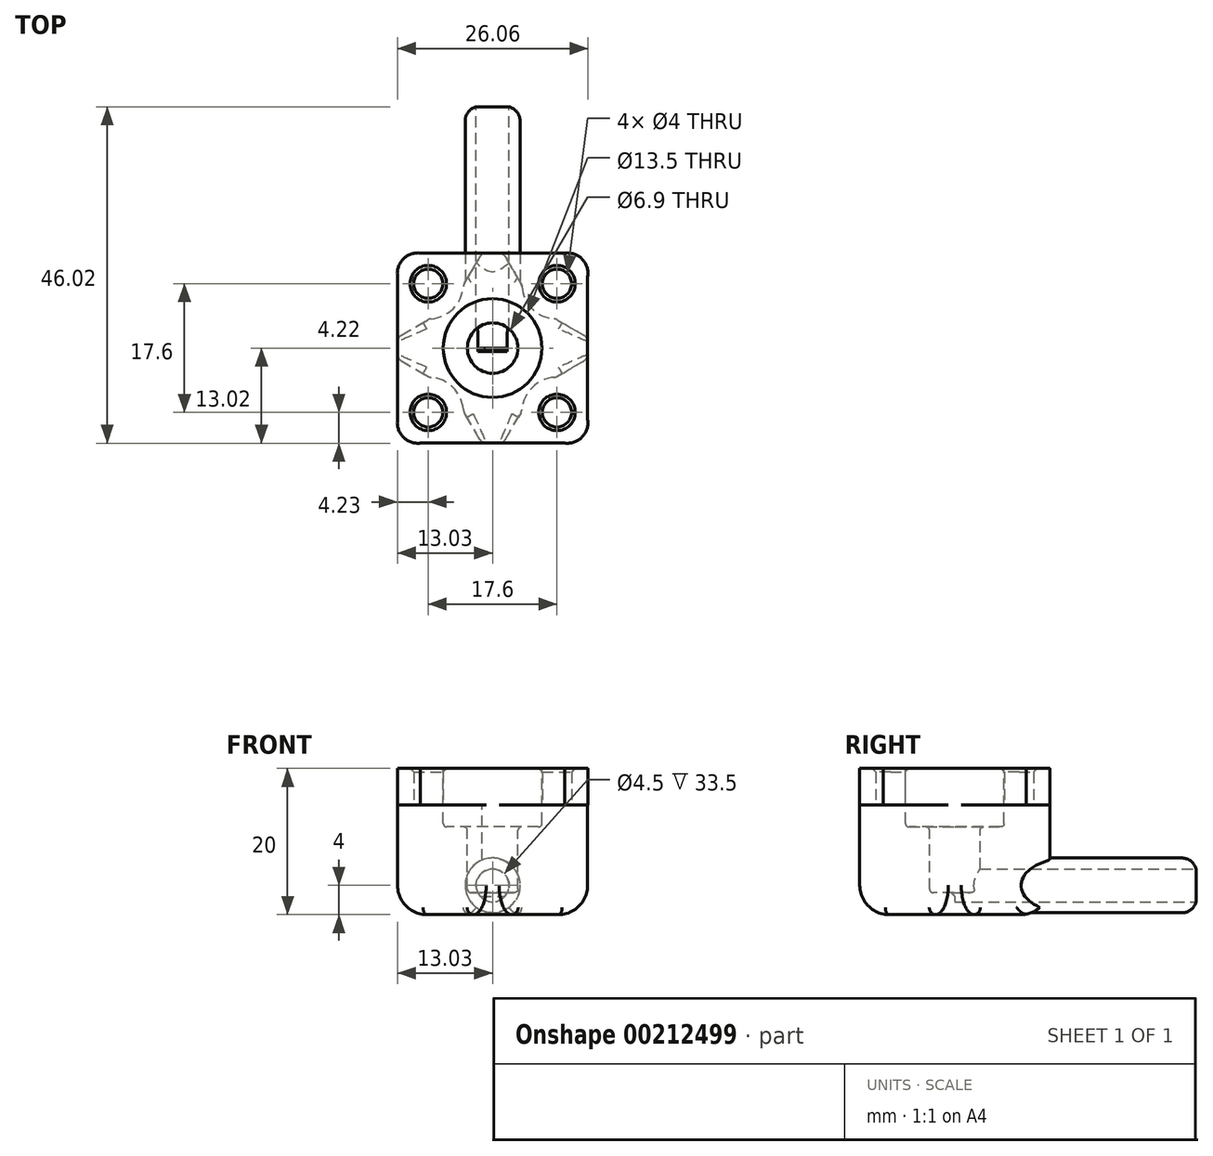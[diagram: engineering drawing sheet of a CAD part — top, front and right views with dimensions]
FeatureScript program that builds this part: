
annotation { "Feature Type Name" : "Feature", "Feature Type Description" : "" }
export const myFeature = defineFeature(function(context is Context, id is Id, definition is map)
    precondition{}
    {
        {
            var Q0;
            Q0=qCreatedBy(makeId("Top.planeOp"),FACE);
            var sketch = newSketch(context, id + "F0", { "sketchPlane" : qUnion([Q0])});
            skLineSegment(sketch, "E0.bottom", {"start": v(-9.87, 13) * mm, "end": v(9.87, 13) * mm});
            skLineSegment(sketch, "E0.top", {"start": v(-9.87, -13) * mm, "end": v(9.87, -13) * mm});
            skLineSegment(sketch, "E0.left", {"start": v(-13, 9.78) * mm, "end": v(-13, -9.78) * mm});
            skLineSegment(sketch, "E0.right", {"start": v(13, 9.78) * mm, "end": v(13, -9.78) * mm});
            skLineSegment(sketch, "E1.bottom", {"start": v(-8.8, 8.8) * mm, "end": v(8.8, 8.8) * mm, "construction": true});
            skLineSegment(sketch, "E1.top", {"start": v(-8.8, -8.8) * mm, "end": v(8.8, -8.8) * mm, "construction": true});
            skLineSegment(sketch, "E1.left", {"start": v(-8.8, 8.8) * mm, "end": v(-8.8, -8.8) * mm, "construction": true});
            skLineSegment(sketch, "E1.right", {"start": v(8.8, 8.8) * mm, "end": v(8.8, -8.8) * mm, "construction": true});
            skCircle(sketch, "E2", {"center": v(-8.8, 8.8) * mm, "radius": 2 * mm});
            skCircle(sketch, "E3", {"center": v(8.8, 8.8) * mm, "radius": 2 * mm});
            skCircle(sketch, "E4", {"center": v(8.8, -8.8) * mm, "radius": 2 * mm});
            skCircle(sketch, "E5", {"center": v(-8.8, -8.8) * mm, "radius": 2 * mm});
            skArc(sketch, "E6", {"start": v(-9.87, 13) * mm, "mid": v(-12.24, 12.17) * mm, "end": v(-13, 9.78) * mm});
            skArc(sketch, "E7.MirrorCS", {"start": v(9.87, 13) * mm, "mid": v(12.24, 12.17) * mm, "end": v(13, 9.78) * mm});
            skArc(sketch, "E8.MirrorCS", {"start": v(-9.87, -13) * mm, "mid": v(-12.24, -12.17) * mm, "end": v(-13, -9.78) * mm});
            skArc(sketch, "E9.MirrorCS", {"start": v(9.87, -13) * mm, "mid": v(12.24, -12.17) * mm, "end": v(13, -9.78) * mm});
            skPoint(sketch, "E10.orphan", {"position": v(13, 13) * mm});
            skPoint(sketch, "E11.orphan", {"position": v(13, -13) * mm});
            skPoint(sketch, "E12.orphan", {"position": v(-13, 13) * mm});
            skPoint(sketch, "E13.orphan", {"position": v(-9.87, 13) * mm});
            skSolve(sketch);
        }
        {
            var Q0;
            Q0 = qSketchRegion(id + "F0", true);
            extrude(context, id + "F1", {"entities" : qUnion([Q0]), "depth" : 20 * mm});
        }
        {
            var Q0;
            Q0=makeQuery(id+"F1.opExtrude","CAP_FACE",FACE,{"disambiguationData":[OSD([sQuery(id+"F0.wireOp",EDGE,"E0.bottom"),sQuery(id+"F0.wireOp",EDGE,"E0.top"),sQuery(id+"F0.wireOp",EDGE,"E0.left"),sQuery(id+"F0.wireOp",EDGE,"E0.right"),sQuery(id+"F0.wireOp",EDGE,"E2"),sQuery(id+"F0.wireOp",EDGE,"E3"),sQuery(id+"F0.wireOp",EDGE,"E4"),sQuery(id+"F0.wireOp",EDGE,"E5"),sQuery(id+"F0.wireOp",EDGE,"E6"),sQuery(id+"F0.wireOp",EDGE,"E7.MirrorCS"),sQuery(id+"F0.wireOp",EDGE,"E8.MirrorCS"),sQuery(id+"F0.wireOp",EDGE,"E9.MirrorCS")])],"isStart":false});
            var sketch = newSketch(context, id + "F2", { "sketchPlane" : qUnion([Q0])});
            skCircle(sketch, "E14", {"center": v(0, 0) * mm, "radius": 3.45 * mm});
            skSolve(sketch);
        }
        {
            var Q0;
            Q0 = qSketchRegion(id + "F2", true);
            extrude(context, id + "F3", {"entities" : qUnion([Q0]), "operationType" : NewBodyOperationType.REMOVE, "oppositeDirection" : true, "depth" : 17 * mm});
        }
        {
            var Q0;
            Q0=makeQuery(id+"F1.opExtrude","CAP_FACE",FACE,{"disambiguationData":[OSD([sQuery(id+"F0.wireOp",EDGE,"E0.bottom"),sQuery(id+"F0.wireOp",EDGE,"E0.top"),sQuery(id+"F0.wireOp",EDGE,"E0.left"),sQuery(id+"F0.wireOp",EDGE,"E0.right"),sQuery(id+"F0.wireOp",EDGE,"E2"),sQuery(id+"F0.wireOp",EDGE,"E3"),sQuery(id+"F0.wireOp",EDGE,"E4"),sQuery(id+"F0.wireOp",EDGE,"E5"),sQuery(id+"F0.wireOp",EDGE,"E6"),sQuery(id+"F0.wireOp",EDGE,"E7.MirrorCS"),sQuery(id+"F0.wireOp",EDGE,"E8.MirrorCS"),sQuery(id+"F0.wireOp",EDGE,"E9.MirrorCS")])],"isStart":false});
            var sketch = newSketch(context, id + "F4", { "sketchPlane" : qUnion([Q0])});
            skCircle(sketch, "E15", {"center": v(0, 0) * mm, "radius": 6.75 * mm});
            skSolve(sketch);
        }
        {
            var Q0;
            Q0 = qSketchRegion(id + "F4", true);
            extrude(context, id + "F5", {"entities" : qUnion([Q0]), "operationType" : NewBodyOperationType.REMOVE, "oppositeDirection" : true, "depth" : 8 * mm});
        }
        {
            var Q0;
            Q0=makeQuery(id+"F1.opExtrude","CAP_FACE",FACE,{"disambiguationData":[OSD([sQuery(id+"F0.wireOp",EDGE,"E0.bottom"),sQuery(id+"F0.wireOp",EDGE,"E0.top"),sQuery(id+"F0.wireOp",EDGE,"E0.left"),sQuery(id+"F0.wireOp",EDGE,"E0.right"),sQuery(id+"F0.wireOp",EDGE,"E2"),sQuery(id+"F0.wireOp",EDGE,"E3"),sQuery(id+"F0.wireOp",EDGE,"E4"),sQuery(id+"F0.wireOp",EDGE,"E5"),sQuery(id+"F0.wireOp",EDGE,"E6"),sQuery(id+"F0.wireOp",EDGE,"E7.MirrorCS"),sQuery(id+"F0.wireOp",EDGE,"E8.MirrorCS"),sQuery(id+"F0.wireOp",EDGE,"E9.MirrorCS")])],"isStart":true});
            var sketch = newSketch(context, id + "F6", { "sketchPlane" : qUnion([Q0])});
            skCircle(sketch, "E16", {"center": v(-8.8, 8.8) * mm, "radius": 4.81 * mm});
            skCircle(sketch, "E17.MirrorC", {"center": v(8.8, 8.8) * mm, "radius": 4.81 * mm});
            skCircle(sketch, "E18.MirrorC", {"center": v(-8.8, -8.8) * mm, "radius": 4.81 * mm});
            skCircle(sketch, "E19.MirrorC", {"center": v(8.8, -8.8) * mm, "radius": 4.81 * mm});
            skSolve(sketch);
        }
        {
            var Q0;
            Q0 = qSketchRegion(id + "F6", true);
            extrude(context, id + "F7", {"entities" : qUnion([Q0]), "operationType" : NewBodyOperationType.REMOVE, "oppositeDirection" : true, "depth" : 30 * mm, "symmetric" : true});
        }
        {
            var Q0;
            Q0=makeQuery(id+"F1.opExtrude","SWEPT_FACE",FACE,{"disambiguationData":[OSD([sQuery(id+"F0.wireOp",EDGE,"E0.bottom")])]});
            var sketch = newSketch(context, id + "F8", { "sketchPlane" : qUnion([Q0])});
            skCircle(sketch, "E20", {"center": v(0, 4) * mm, "radius": 3.75 * mm});
            skSolve(sketch);
        }
        {
            var Q0;
            Q0 = qSketchRegion(id + "F8", true);
            extrude(context, id + "F9", {"entities" : qUnion([Q0]), "operationType" : NewBodyOperationType.ADD, "depth" : 20 * mm});
        }
        {
            var Q0;
            Q0=makeQuery(id+"F9.opExtrude","CAP_FACE",FACE,{"disambiguationData":[OSD([sQuery(id+"F8.wireOp",EDGE,"E20")])],"isStart":false});
            var sketch = newSketch(context, id + "F10", { "sketchPlane" : qUnion([Q0])});
            skCircle(sketch, "E21", {"center": v(0, 4) * mm, "radius": 2.25 * mm});
            skSolve(sketch);
        }
        {
            var Q0;
            Q0 = qSketchRegion(id + "F10", true);
            extrude(context, id + "F11", {"entities" : qUnion([Q0]), "operationType" : NewBodyOperationType.REMOVE, "oppositeDirection" : true, "depth" : 33 * mm});
        }
        {
            var Q0;
            Q0=makeQuery(id+"F7.boolean.opBoolean","INTERSECT",EDGE,{"derivedFrom":[makeQuery(id+"F1.opExtrude","SWEPT_FACE",FACE,{"disambiguationData":[OSD([sQuery(id+"F0.wireOp",EDGE,"E0.left")])]}),makeQuery(id+"F7.opExtrude","SWEPT_FACE",FACE,{"disambiguationData":[OSD([sQuery(id+"F6.wireOp",EDGE,"E16")])]})]});
            var Q1;
            Q1=makeQuery(id+"F7.boolean.opBoolean","INTERSECT",EDGE,{"derivedFrom":[makeQuery(id+"F1.opExtrude","SWEPT_FACE",FACE,{"disambiguationData":[OSD([sQuery(id+"F0.wireOp",EDGE,"E0.left")])]}),makeQuery(id+"F7.opExtrude","SWEPT_FACE",FACE,{"disambiguationData":[OSD([sQuery(id+"F6.wireOp",EDGE,"E18.MirrorC")])]})]});
            var Q2;
            Q2=makeQuery(id+"F7.boolean.opBoolean","INTERSECT",EDGE,{"derivedFrom":[makeQuery(id+"F1.opExtrude","SWEPT_FACE",FACE,{"disambiguationData":[OSD([sQuery(id+"F0.wireOp",EDGE,"E0.right")])]}),makeQuery(id+"F7.opExtrude","SWEPT_FACE",FACE,{"disambiguationData":[OSD([sQuery(id+"F6.wireOp",EDGE,"E17.MirrorC")])]})]});
            var Q3;
            Q3=makeQuery(id+"F7.boolean.opBoolean","INTERSECT",EDGE,{"derivedFrom":[makeQuery(id+"F1.opExtrude","SWEPT_FACE",FACE,{"disambiguationData":[OSD([sQuery(id+"F0.wireOp",EDGE,"E0.bottom")])]}),makeQuery(id+"F7.opExtrude","SWEPT_FACE",FACE,{"disambiguationData":[OSD([sQuery(id+"F6.wireOp",EDGE,"E18.MirrorC")])]})]});
            var Q4;
            Q4=makeQuery(id+"F7.boolean.opBoolean","INTERSECT",EDGE,{"derivedFrom":[makeQuery(id+"F1.opExtrude","SWEPT_FACE",FACE,{"disambiguationData":[OSD([sQuery(id+"F0.wireOp",EDGE,"E0.bottom")])]}),makeQuery(id+"F7.opExtrude","SWEPT_FACE",FACE,{"disambiguationData":[OSD([sQuery(id+"F6.wireOp",EDGE,"E19.MirrorC")])]})]});
            var Q5;
            Q5=makeQuery(id+"F7.boolean.opBoolean","INTERSECT",EDGE,{"derivedFrom":[makeQuery(id+"F1.opExtrude","SWEPT_FACE",FACE,{"disambiguationData":[OSD([sQuery(id+"F0.wireOp",EDGE,"E0.right")])]}),makeQuery(id+"F7.opExtrude","SWEPT_FACE",FACE,{"disambiguationData":[OSD([sQuery(id+"F6.wireOp",EDGE,"E19.MirrorC")])]})]});
            var Q6;
            Q6=makeQuery(id+"F7.boolean.opBoolean","INTERSECT",EDGE,{"derivedFrom":[makeQuery(id+"F1.opExtrude","SWEPT_FACE",FACE,{"disambiguationData":[OSD([sQuery(id+"F0.wireOp",EDGE,"E0.top")])]}),makeQuery(id+"F7.opExtrude","SWEPT_FACE",FACE,{"disambiguationData":[OSD([sQuery(id+"F6.wireOp",EDGE,"E16")])]})]});
            var Q7;
            Q7=makeQuery(id+"F7.boolean.opBoolean","INTERSECT",EDGE,{"derivedFrom":[makeQuery(id+"F1.opExtrude","SWEPT_FACE",FACE,{"disambiguationData":[OSD([sQuery(id+"F0.wireOp",EDGE,"E0.top")])]}),makeQuery(id+"F7.opExtrude","SWEPT_FACE",FACE,{"disambiguationData":[OSD([sQuery(id+"F6.wireOp",EDGE,"E17.MirrorC")])]})]});
            chamfer(context, id + "F12", {"entities" : qUnion([Q0, Q1, Q2, Q3, Q4, Q5, Q6, Q7]), "width" : 5 * mm, "tangentPropagation" : true});
        }
        {
            var Q0;
            Q0=makeQuery(id+"F1.opExtrude","CAP_EDGE",EDGE,{"disambiguationData":[OSD([sQuery(id+"F0.wireOp",EDGE,"E0.right")])],"isStart":true});
            var Q1;
            Q1=makeQuery(id+"F1.opExtrude","CAP_EDGE",EDGE,{"disambiguationData":[OSD([sQuery(id+"F0.wireOp",EDGE,"E0.top")])],"isStart":true});
            var Q2;
            Q2=makeQuery(id+"F1.opExtrude","CAP_EDGE",EDGE,{"disambiguationData":[OSD([sQuery(id+"F0.wireOp",EDGE,"E0.left")])],"isStart":true});
            var Q3;
            Q3=makeQuery(id+"F1.opExtrude","CAP_EDGE",EDGE,{"disambiguationData":[OSD([sQuery(id+"F0.wireOp",EDGE,"E0.bottom")])],"isStart":true});
            fillet(context, id + "F13", {"entities" : qUnion([Q0, Q1, Q2, Q3]), "radius" : 4 * mm, "tangentPropagation" : true, "allowEdgeOverflow" : false});
        }
        {
            var Q0;
            Q0=makeQuery(id+"F9.opExtrude","CAP_EDGE",EDGE,{"disambiguationData":[OSD([sQuery(id+"F8.wireOp",EDGE,"E20")])],"isStart":false});
            fillet(context, id + "F14", {"entities" : qUnion([Q0]), "radius" : 2 * mm, "tangentPropagation" : true, "allowEdgeOverflow" : false});
        }
        {
            var Q0;
            {var subQ0=makeQuery(id+"F1.opExtrude","SWEPT_FACE",FACE,{"disambiguationData":[OSD([sQuery(id+"F0.wireOp",EDGE,"E0.left")])]});Q0=makeQuery(id+"F12.opChamfer","BLEND_EDGE",EDGE,{"blendedFrom":[makeQuery(id+"F7.boolean.opBoolean","INTERSECT",EDGE,{"derivedFrom":[subQ0,makeQuery(id+"F7.opExtrude","SWEPT_FACE",FACE,{"disambiguationData":[OSD([sQuery(id+"F6.wireOp",EDGE,"E18.MirrorC")])]})]}),subQ0],"blendedInto":[subQ0]});}
            var Q1;
            {var subQ0=makeQuery(id+"F1.opExtrude","SWEPT_FACE",FACE,{"disambiguationData":[OSD([sQuery(id+"F0.wireOp",EDGE,"E0.left")])]});Q1=makeQuery(id+"F12.opChamfer","BLEND_EDGE",EDGE,{"blendedFrom":[makeQuery(id+"F7.boolean.opBoolean","INTERSECT",EDGE,{"derivedFrom":[subQ0,makeQuery(id+"F7.opExtrude","SWEPT_FACE",FACE,{"disambiguationData":[OSD([sQuery(id+"F6.wireOp",EDGE,"E16")])]})]}),subQ0],"blendedInto":[subQ0]});}
            var Q2;
            {var subQ0=makeQuery(id+"F7.opExtrude","SWEPT_FACE",FACE,{"disambiguationData":[OSD([sQuery(id+"F6.wireOp",EDGE,"E18.MirrorC")])]});Q2=makeQuery(id+"F12.opChamfer","BLEND_EDGE",EDGE,{"blendedFrom":[makeQuery(id+"F7.boolean.opBoolean","INTERSECT",EDGE,{"derivedFrom":[makeQuery(id+"F1.opExtrude","SWEPT_FACE",FACE,{"disambiguationData":[OSD([sQuery(id+"F0.wireOp",EDGE,"E0.bottom")])]}),subQ0]}),makeQuery(id+"F7.boolean.opBoolean","COPY",FACE,{"derivedFrom":subQ0})],"blendedInto":[makeQuery(id+"F7.boolean.opBoolean","COPY",FACE,{"derivedFrom":subQ0})]});}
            var Q3;
            {var subQ0=makeQuery(id+"F1.opExtrude","SWEPT_FACE",FACE,{"disambiguationData":[OSD([sQuery(id+"F0.wireOp",EDGE,"E0.top")])]});Q3=makeQuery(id+"F12.opChamfer","BLEND_EDGE",EDGE,{"blendedFrom":[makeQuery(id+"F7.boolean.opBoolean","INTERSECT",EDGE,{"derivedFrom":[subQ0,makeQuery(id+"F7.opExtrude","SWEPT_FACE",FACE,{"disambiguationData":[OSD([sQuery(id+"F6.wireOp",EDGE,"E16")])]})]}),subQ0],"blendedInto":[subQ0]});}
            var Q4;
            {var subQ0=makeQuery(id+"F1.opExtrude","SWEPT_FACE",FACE,{"disambiguationData":[OSD([sQuery(id+"F0.wireOp",EDGE,"E0.top")])]});Q4=makeQuery(id+"F12.opChamfer","BLEND_EDGE",EDGE,{"blendedFrom":[makeQuery(id+"F7.boolean.opBoolean","INTERSECT",EDGE,{"derivedFrom":[subQ0,makeQuery(id+"F7.opExtrude","SWEPT_FACE",FACE,{"disambiguationData":[OSD([sQuery(id+"F6.wireOp",EDGE,"E17.MirrorC")])]})]}),subQ0],"blendedInto":[subQ0]});}
            var Q5;
            {var subQ0=makeQuery(id+"F1.opExtrude","SWEPT_FACE",FACE,{"disambiguationData":[OSD([sQuery(id+"F0.wireOp",EDGE,"E0.right")])]});Q5=makeQuery(id+"F12.opChamfer","BLEND_EDGE",EDGE,{"blendedFrom":[makeQuery(id+"F7.boolean.opBoolean","INTERSECT",EDGE,{"derivedFrom":[subQ0,makeQuery(id+"F7.opExtrude","SWEPT_FACE",FACE,{"disambiguationData":[OSD([sQuery(id+"F6.wireOp",EDGE,"E17.MirrorC")])]})]}),subQ0],"blendedInto":[subQ0]});}
            var Q6;
            {var subQ0=makeQuery(id+"F1.opExtrude","SWEPT_FACE",FACE,{"disambiguationData":[OSD([sQuery(id+"F0.wireOp",EDGE,"E0.right")])]});Q6=makeQuery(id+"F12.opChamfer","BLEND_EDGE",EDGE,{"blendedFrom":[makeQuery(id+"F7.boolean.opBoolean","INTERSECT",EDGE,{"derivedFrom":[subQ0,makeQuery(id+"F7.opExtrude","SWEPT_FACE",FACE,{"disambiguationData":[OSD([sQuery(id+"F6.wireOp",EDGE,"E19.MirrorC")])]})]}),subQ0],"blendedInto":[subQ0]});}
            var Q7;
            {var subQ0=makeQuery(id+"F1.opExtrude","SWEPT_FACE",FACE,{"disambiguationData":[OSD([sQuery(id+"F0.wireOp",EDGE,"E0.bottom")])]});Q7=makeQuery(id+"F12.opChamfer","BLEND_EDGE",EDGE,{"disambiguationData":[OD(0.0)],"blendedFrom":[makeQuery(id+"F7.boolean.opBoolean","INTERSECT",EDGE,{"derivedFrom":[subQ0,makeQuery(id+"F7.opExtrude","SWEPT_FACE",FACE,{"disambiguationData":[OSD([sQuery(id+"F6.wireOp",EDGE,"E19.MirrorC")])]})]}),subQ0],"blendedInto":[subQ0]});}
            var Q8;
            {var subQ0=makeQuery(id+"F7.opExtrude","SWEPT_FACE",FACE,{"disambiguationData":[OSD([sQuery(id+"F6.wireOp",EDGE,"E16")])]});Q8=makeQuery(id+"F12.opChamfer","BLEND_EDGE",EDGE,{"blendedFrom":[makeQuery(id+"F7.boolean.opBoolean","INTERSECT",EDGE,{"derivedFrom":[makeQuery(id+"F1.opExtrude","SWEPT_FACE",FACE,{"disambiguationData":[OSD([sQuery(id+"F0.wireOp",EDGE,"E0.left")])]}),subQ0]}),makeQuery(id+"F7.boolean.opBoolean","COPY",FACE,{"derivedFrom":subQ0})],"blendedInto":[makeQuery(id+"F7.boolean.opBoolean","COPY",FACE,{"derivedFrom":subQ0})]});}
            var Q9;
            {var subQ0=makeQuery(id+"F7.opExtrude","SWEPT_FACE",FACE,{"disambiguationData":[OSD([sQuery(id+"F6.wireOp",EDGE,"E16")])]});Q9=makeQuery(id+"F12.opChamfer","BLEND_EDGE",EDGE,{"blendedFrom":[makeQuery(id+"F7.boolean.opBoolean","INTERSECT",EDGE,{"derivedFrom":[makeQuery(id+"F1.opExtrude","SWEPT_FACE",FACE,{"disambiguationData":[OSD([sQuery(id+"F0.wireOp",EDGE,"E0.top")])]}),subQ0]}),makeQuery(id+"F7.boolean.opBoolean","COPY",FACE,{"derivedFrom":subQ0})],"blendedInto":[makeQuery(id+"F7.boolean.opBoolean","COPY",FACE,{"derivedFrom":subQ0})]});}
            var Q10;
            {var subQ0=makeQuery(id+"F7.opExtrude","SWEPT_FACE",FACE,{"disambiguationData":[OSD([sQuery(id+"F6.wireOp",EDGE,"E17.MirrorC")])]});Q10=makeQuery(id+"F12.opChamfer","BLEND_EDGE",EDGE,{"blendedFrom":[makeQuery(id+"F7.boolean.opBoolean","INTERSECT",EDGE,{"derivedFrom":[makeQuery(id+"F1.opExtrude","SWEPT_FACE",FACE,{"disambiguationData":[OSD([sQuery(id+"F0.wireOp",EDGE,"E0.right")])]}),subQ0]}),makeQuery(id+"F7.boolean.opBoolean","COPY",FACE,{"derivedFrom":subQ0})],"blendedInto":[makeQuery(id+"F7.boolean.opBoolean","COPY",FACE,{"derivedFrom":subQ0})]});}
            var Q11;
            {var subQ0=makeQuery(id+"F7.opExtrude","SWEPT_FACE",FACE,{"disambiguationData":[OSD([sQuery(id+"F6.wireOp",EDGE,"E17.MirrorC")])]});Q11=makeQuery(id+"F12.opChamfer","BLEND_EDGE",EDGE,{"blendedFrom":[makeQuery(id+"F7.boolean.opBoolean","INTERSECT",EDGE,{"derivedFrom":[makeQuery(id+"F1.opExtrude","SWEPT_FACE",FACE,{"disambiguationData":[OSD([sQuery(id+"F0.wireOp",EDGE,"E0.top")])]}),subQ0]}),makeQuery(id+"F7.boolean.opBoolean","COPY",FACE,{"derivedFrom":subQ0})],"blendedInto":[makeQuery(id+"F7.boolean.opBoolean","COPY",FACE,{"derivedFrom":subQ0})]});}
            var Q12;
            {var subQ0=makeQuery(id+"F7.opExtrude","SWEPT_FACE",FACE,{"disambiguationData":[OSD([sQuery(id+"F6.wireOp",EDGE,"E19.MirrorC")])]});Q12=makeQuery(id+"F12.opChamfer","BLEND_EDGE",EDGE,{"blendedFrom":[makeQuery(id+"F7.boolean.opBoolean","INTERSECT",EDGE,{"derivedFrom":[makeQuery(id+"F1.opExtrude","SWEPT_FACE",FACE,{"disambiguationData":[OSD([sQuery(id+"F0.wireOp",EDGE,"E0.right")])]}),subQ0]}),makeQuery(id+"F7.boolean.opBoolean","COPY",FACE,{"derivedFrom":subQ0})],"blendedInto":[makeQuery(id+"F7.boolean.opBoolean","COPY",FACE,{"derivedFrom":subQ0})]});}
            var Q13;
            {var subQ0=makeQuery(id+"F7.opExtrude","SWEPT_FACE",FACE,{"disambiguationData":[OSD([sQuery(id+"F6.wireOp",EDGE,"E19.MirrorC")])]});Q13=makeQuery(id+"F12.opChamfer","BLEND_EDGE",EDGE,{"blendedFrom":[makeQuery(id+"F7.boolean.opBoolean","INTERSECT",EDGE,{"derivedFrom":[makeQuery(id+"F1.opExtrude","SWEPT_FACE",FACE,{"disambiguationData":[OSD([sQuery(id+"F0.wireOp",EDGE,"E0.bottom")])]}),subQ0]}),makeQuery(id+"F7.boolean.opBoolean","COPY",FACE,{"derivedFrom":subQ0})],"blendedInto":[makeQuery(id+"F7.boolean.opBoolean","COPY",FACE,{"derivedFrom":subQ0})]});}
            var Q14;
            {var subQ0=makeQuery(id+"F7.opExtrude","SWEPT_FACE",FACE,{"disambiguationData":[OSD([sQuery(id+"F6.wireOp",EDGE,"E18.MirrorC")])]});Q14=makeQuery(id+"F12.opChamfer","BLEND_EDGE",EDGE,{"blendedFrom":[makeQuery(id+"F7.boolean.opBoolean","INTERSECT",EDGE,{"derivedFrom":[makeQuery(id+"F1.opExtrude","SWEPT_FACE",FACE,{"disambiguationData":[OSD([sQuery(id+"F0.wireOp",EDGE,"E0.left")])]}),subQ0]}),makeQuery(id+"F7.boolean.opBoolean","COPY",FACE,{"derivedFrom":subQ0})],"blendedInto":[makeQuery(id+"F7.boolean.opBoolean","COPY",FACE,{"derivedFrom":subQ0})]});}
            var Q15;
            Q15=makeQuery(id+"F7.boolean.opBoolean","INTERSECT",EDGE,{"derivedFrom":[makeQuery(id+"F1.opExtrude","CAP_FACE",FACE,{"disambiguationData":[OSD([sQuery(id+"F0.wireOp",EDGE,"E0.bottom"),sQuery(id+"F0.wireOp",EDGE,"E0.top"),sQuery(id+"F0.wireOp",EDGE,"E0.left"),sQuery(id+"F0.wireOp",EDGE,"E0.right"),sQuery(id+"F0.wireOp",EDGE,"E2"),sQuery(id+"F0.wireOp",EDGE,"E3"),sQuery(id+"F0.wireOp",EDGE,"E4"),sQuery(id+"F0.wireOp",EDGE,"E5"),sQuery(id+"F0.wireOp",EDGE,"E6"),sQuery(id+"F0.wireOp",EDGE,"E7.MirrorCS"),sQuery(id+"F0.wireOp",EDGE,"E8.MirrorCS"),sQuery(id+"F0.wireOp",EDGE,"E9.MirrorCS")])],"isStart":true}),makeQuery(id+"F7.opExtrude","SWEPT_FACE",FACE,{"disambiguationData":[OSD([sQuery(id+"F6.wireOp",EDGE,"E16")])]})]});
            var Q16;
            Q16=makeQuery(id+"F7.boolean.opBoolean","INTERSECT",EDGE,{"derivedFrom":[makeQuery(id+"F1.opExtrude","CAP_FACE",FACE,{"disambiguationData":[OSD([sQuery(id+"F0.wireOp",EDGE,"E0.bottom"),sQuery(id+"F0.wireOp",EDGE,"E0.top"),sQuery(id+"F0.wireOp",EDGE,"E0.left"),sQuery(id+"F0.wireOp",EDGE,"E0.right"),sQuery(id+"F0.wireOp",EDGE,"E2"),sQuery(id+"F0.wireOp",EDGE,"E3"),sQuery(id+"F0.wireOp",EDGE,"E4"),sQuery(id+"F0.wireOp",EDGE,"E5"),sQuery(id+"F0.wireOp",EDGE,"E6"),sQuery(id+"F0.wireOp",EDGE,"E7.MirrorCS"),sQuery(id+"F0.wireOp",EDGE,"E8.MirrorCS"),sQuery(id+"F0.wireOp",EDGE,"E9.MirrorCS")])],"isStart":true}),makeQuery(id+"F7.opExtrude","SWEPT_FACE",FACE,{"disambiguationData":[OSD([sQuery(id+"F6.wireOp",EDGE,"E18.MirrorC")])]})]});
            var Q17;
            Q17=makeQuery(id+"F7.boolean.opBoolean","INTERSECT",EDGE,{"derivedFrom":[makeQuery(id+"F1.opExtrude","CAP_FACE",FACE,{"disambiguationData":[OSD([sQuery(id+"F0.wireOp",EDGE,"E0.bottom"),sQuery(id+"F0.wireOp",EDGE,"E0.top"),sQuery(id+"F0.wireOp",EDGE,"E0.left"),sQuery(id+"F0.wireOp",EDGE,"E0.right"),sQuery(id+"F0.wireOp",EDGE,"E2"),sQuery(id+"F0.wireOp",EDGE,"E3"),sQuery(id+"F0.wireOp",EDGE,"E4"),sQuery(id+"F0.wireOp",EDGE,"E5"),sQuery(id+"F0.wireOp",EDGE,"E6"),sQuery(id+"F0.wireOp",EDGE,"E7.MirrorCS"),sQuery(id+"F0.wireOp",EDGE,"E8.MirrorCS"),sQuery(id+"F0.wireOp",EDGE,"E9.MirrorCS")])],"isStart":true}),makeQuery(id+"F7.opExtrude","SWEPT_FACE",FACE,{"disambiguationData":[OSD([sQuery(id+"F6.wireOp",EDGE,"E19.MirrorC")])]})]});
            var Q18;
            Q18=makeQuery(id+"F7.boolean.opBoolean","INTERSECT",EDGE,{"derivedFrom":[makeQuery(id+"F1.opExtrude","CAP_FACE",FACE,{"disambiguationData":[OSD([sQuery(id+"F0.wireOp",EDGE,"E0.bottom"),sQuery(id+"F0.wireOp",EDGE,"E0.top"),sQuery(id+"F0.wireOp",EDGE,"E0.left"),sQuery(id+"F0.wireOp",EDGE,"E0.right"),sQuery(id+"F0.wireOp",EDGE,"E2"),sQuery(id+"F0.wireOp",EDGE,"E3"),sQuery(id+"F0.wireOp",EDGE,"E4"),sQuery(id+"F0.wireOp",EDGE,"E5"),sQuery(id+"F0.wireOp",EDGE,"E6"),sQuery(id+"F0.wireOp",EDGE,"E7.MirrorCS"),sQuery(id+"F0.wireOp",EDGE,"E8.MirrorCS"),sQuery(id+"F0.wireOp",EDGE,"E9.MirrorCS")])],"isStart":true}),makeQuery(id+"F7.opExtrude","SWEPT_FACE",FACE,{"disambiguationData":[OSD([sQuery(id+"F6.wireOp",EDGE,"E17.MirrorC")])]})]});
            fillet(context, id + "F15", {"entities" : qUnion([Q0, Q1, Q2, Q3, Q4, Q5, Q6, Q7, Q8, Q9, Q10, Q11, Q12, Q13, Q14, Q15, Q16, Q17, Q18]), "radius" : 1 * mm, "tangentPropagation" : true, "allowEdgeOverflow" : false});
        }
        {
            var Q0;
            Q0=makeQuery(id+"F11.boolean.opBoolean","INTERSECT",EDGE,{"derivedFrom":[makeQuery(id+"F3.boolean.opBoolean","COPY",FACE,{"derivedFrom":makeQuery(id+"F3.opExtrude","CAP_FACE",FACE,{"disambiguationData":[OSD([sQuery(id+"F2.wireOp",EDGE,"E14")])],"isStart":false})}),makeQuery(id+"F11.opExtrude","CAP_FACE",FACE,{"disambiguationData":[OSD([sQuery(id+"F10.wireOp",EDGE,"E21")])],"isStart":false})]});
            var Q1;
            Q1=makeQuery(id+"F5.boolean.opBoolean","COPY",EDGE,{"derivedFrom":makeQuery(id+"F5.opExtrude","CAP_EDGE",EDGE,{"disambiguationData":[OSD([sQuery(id+"F4.wireOp",EDGE,"E15")])],"isStart":true})});
            var Q2;
            Q2=makeQuery(id+"F1.opExtrude","CAP_EDGE",EDGE,{"disambiguationData":[OSD([sQuery(id+"F0.wireOp",EDGE,"E2")])],"isStart":false});
            var Q3;
            Q3=makeQuery(id+"F1.opExtrude","CAP_EDGE",EDGE,{"disambiguationData":[OSD([sQuery(id+"F0.wireOp",EDGE,"E3")])],"isStart":false});
            var Q4;
            Q4=makeQuery(id+"F1.opExtrude","CAP_EDGE",EDGE,{"disambiguationData":[OSD([sQuery(id+"F0.wireOp",EDGE,"E5")])],"isStart":false});
            var Q5;
            Q5=makeQuery(id+"F1.opExtrude","CAP_EDGE",EDGE,{"disambiguationData":[OSD([sQuery(id+"F0.wireOp",EDGE,"E4")])],"isStart":false});
            chamfer(context, id + "F16", {"entities" : qUnion([Q0, Q1, Q2, Q3, Q4, Q5]), "width" : .5 * mm, "tangentPropagation" : true});
        }
        {
            var Q0;
            Q0=makeQuery(id+"F5.boolean.opBoolean","INTERSECT",EDGE,{"derivedFrom":[makeQuery(id+"F3.boolean.opBoolean","COPY",FACE,{"derivedFrom":makeQuery(id+"F3.opExtrude","SWEPT_FACE",FACE,{"disambiguationData":[OSD([sQuery(id+"F2.wireOp",EDGE,"E14")])]})}),makeQuery(id+"F5.opExtrude","CAP_FACE",FACE,{"disambiguationData":[OSD([sQuery(id+"F4.wireOp",EDGE,"E15")])],"isStart":false})]});
            var Q1;
            Q1=makeQuery(id+"F3.boolean.opBoolean","COPY",EDGE,{"derivedFrom":makeQuery(id+"F3.opExtrude","CAP_EDGE",EDGE,{"disambiguationData":[OSD([sQuery(id+"F2.wireOp",EDGE,"E14")])],"isStart":false})});
            var Q2;
            Q2=makeQuery(id+"F5.boolean.opBoolean","COPY",EDGE,{"derivedFrom":makeQuery(id+"F5.opExtrude","CAP_EDGE",EDGE,{"disambiguationData":[OSD([sQuery(id+"F4.wireOp",EDGE,"E15")])],"isStart":false})});
            fillet(context, id + "F17", {"entities" : qUnion([Q0, Q1, Q2]), "radius" : .5 * mm, "tangentPropagation" : true, "allowEdgeOverflow" : false});
        }
    });
